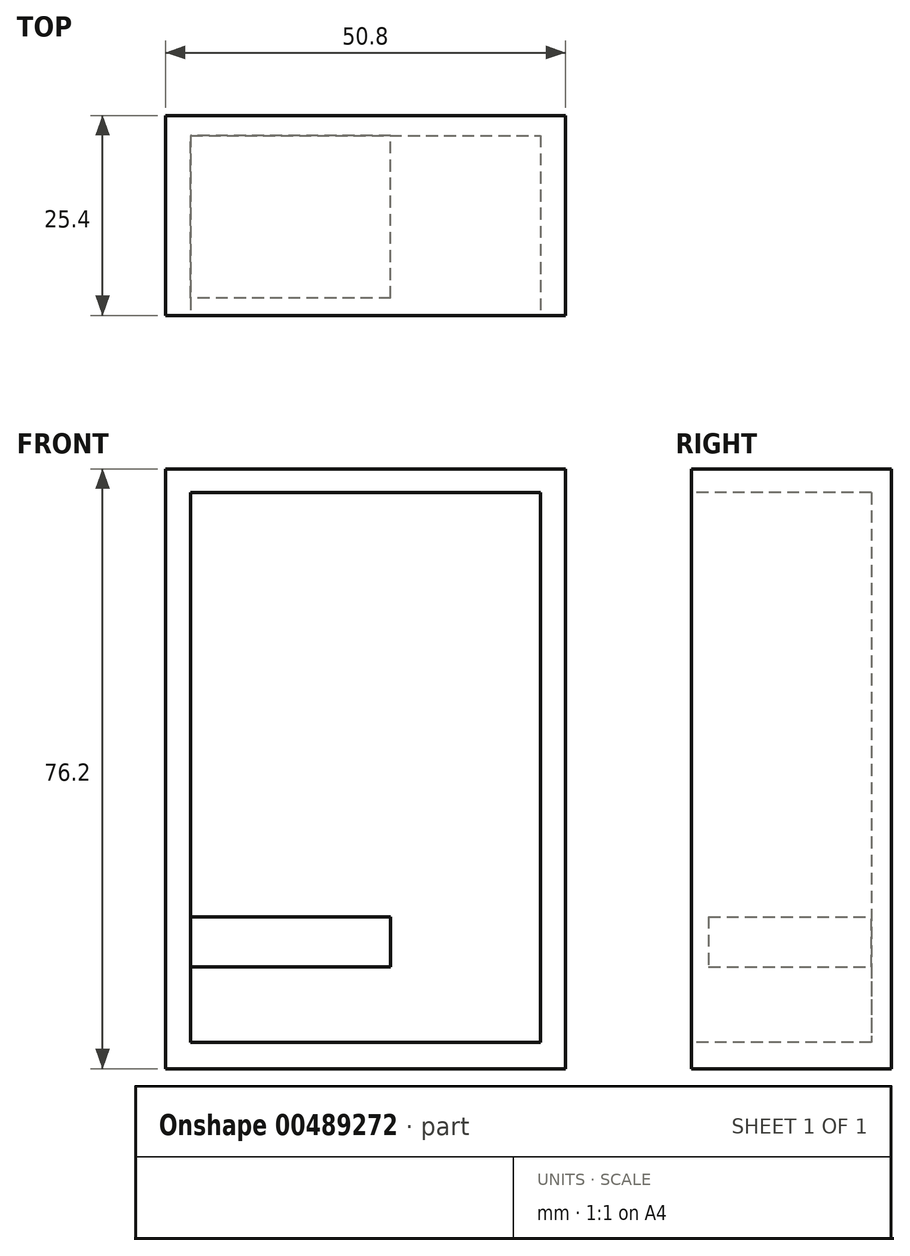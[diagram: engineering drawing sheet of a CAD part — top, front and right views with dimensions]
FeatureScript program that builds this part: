
annotation { "Feature Type Name" : "Feature", "Feature Type Description" : "" }
export const myFeature = defineFeature(function(context is Context, id is Id, definition is map)
    precondition{}
    {
        {
            var Q0;
            Q0=qCreatedBy(makeId("Front.planeOp"),FACE);
            var sketch = newSketch(context, id + "F0", { "sketchPlane" : qUnion([Q0])});
            skLineSegment(sketch, "E0.bottom", {"start": v(0, 0) * mm, "end": v(-50.8, 0) * mm});
            skLineSegment(sketch, "E0.top", {"start": v(0, 76.2) * mm, "end": v(-50.8, 76.2) * mm});
            skLineSegment(sketch, "E0.left", {"start": v(0, 0) * mm, "end": v(0, 76.2) * mm});
            skLineSegment(sketch, "E0.right", {"start": v(-50.8, 0) * mm, "end": v(-50.8, 76.2) * mm});
            skSolve(sketch);
        }
        {
            var Q0;
            Q0 = qSketchRegion(id + "F0", true);
            extrude(context, id + "F1", {"entities" : qUnion([Q0]), "depth" : 25.4 * mm});
        }
        {
            var Q0;
            Q0=makeQuery(id+"F1.opExtrude","CAP_FACE",FACE,{"disambiguationData":[OSD([sQuery(id+"F0.wireOp",EDGE,"E0.bottom"),sQuery(id+"F0.wireOp",EDGE,"E0.top"),sQuery(id+"F0.wireOp",EDGE,"E0.left"),sQuery(id+"F0.wireOp",EDGE,"E0.right")])],"isStart":false});
            var sketch = newSketch(context, id + "F2", { "sketchPlane" : qUnion([Q0])});
            skLineSegment(sketch, "E1.bottom", {"start": v(-47.6, 73.18) * mm, "end": v(-3.16, 73.18) * mm});
            skLineSegment(sketch, "E1.top", {"start": v(-47.6, 3.33) * mm, "end": v(-3.16, 3.33) * mm});
            skLineSegment(sketch, "E1.left", {"start": v(-47.6, 73.18) * mm, "end": v(-47.6, 3.33) * mm});
            skLineSegment(sketch, "E1.right", {"start": v(-3.16, 73.18) * mm, "end": v(-3.16, 3.33) * mm});
            skSolve(sketch);
        }
        {
            var Q0;
            Q0 = qSketchRegion(id + "F2", true);
            extrude(context, id + "F3", {"entities" : qUnion([Q0]), "operationType" : NewBodyOperationType.REMOVE, "oppositeDirection" : true, "depth" : 22.86 * mm});
        }
        {
            var Q0;
            Q0=makeQuery(id+"F3.boolean.opBoolean","COPY",FACE,{"derivedFrom":makeQuery(id+"F3.opExtrude","SWEPT_FACE",FACE,{"disambiguationData":[OSD([sQuery(id+"F2.wireOp",EDGE,"E1.left")])]})});
            var sketch = newSketch(context, id + "F4", { "sketchPlane" : qUnion([Q0])});
            skLineSegment(sketch, "E2.bottom", {"start": v(-23.21, 19.3) * mm, "end": v(-0.35, 19.3) * mm});
            skLineSegment(sketch, "E2.top", {"start": v(-23.21, 12.96) * mm, "end": v(-0.35, 12.96) * mm});
            skLineSegment(sketch, "E2.left", {"start": v(-23.21, 19.3) * mm, "end": v(-23.21, 12.96) * mm});
            skLineSegment(sketch, "E2.right", {"start": v(-0.35, 19.3) * mm, "end": v(-0.35, 12.96) * mm});
            skSolve(sketch);
        }
        {
            var Q0;
            Q0 = qSketchRegion(id + "F4", true);
            extrude(context, id + "F5", {"entities" : qUnion([Q0]), "operationType" : NewBodyOperationType.ADD, "depth" : 25.4 * mm});
        }
    });
